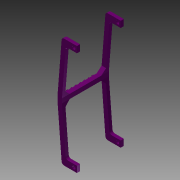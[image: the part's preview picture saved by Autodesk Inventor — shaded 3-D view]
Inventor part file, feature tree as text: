
AUTODESK INVENTOR PART (.ipt)
format: ipt  version: 2015 (Build 190159000, 159)  size: 382,464 bytes
history: native  units: mm
features: extrude x6, sketch x6, plane x2, mirror x2, fillet x1, projected_geometry x1
ambient origin geometry x8: Origin, YZ Plane, XZ Plane, XY Plane, X Axis, Y Axis, Z Axis, Center Point
bodies: Solid1 (feature_tree)
feature tree (18):
  extrude  "Extrusion1"  Depth=3.5mm
  extrude  "Extrusion2"  Depth=3.5mm
  fillet  "Fillet1"  Radius=3.5mm
  plane  "Work Plane2"
  extrude  "Extrusion3"  Depth=4.983674mm
  extrude  "Extrusion4"  Depth=2.5mm
  extrude  "Extrusion5"  Depth=2.5mm
  plane  "Work Plane3"
  mirror  "Mirror1"
  mirror  "Mirror2"
  extrude  "Extrusion6"  Depth=30.607599mm
  sketch  "Sketch3"  dims[d0=7.0mm d1=3.5mm]
  sketch  "Sketch4"  dims[d2=7.0mm d8=3.5mm d9=3.5mm]
  sketch  "Sketch6"  dims[d13=9.917653mm d14=4.983674mm]
  sketch  "Sketch7"  dims[d15=8.285585mm d17=2.5mm]
  sketch  "Sketch8"  dims[d18=90.0deg d19=2.5mm]
  sketch  "Sketch9"  dims[d21=5.0mm d22=30.607599mm d24=56.462921mm d25=49.462921mm d26=30.607599mm d27=16.516291mm d28=16.516291mm d29=2.8mm d30=2.8mm d31=5.0mm d32=3.5mm d33=0.0mm d34=5.0mm d35=5.0mm d36=22.75mm d37=0.0mm d38=0.25mm d40=-23.58913mm d41=5.0mm d42=0.0mm d43=45.0deg d44=7.0mm d45=0.0mm d46=7.0mm d47=0.0mm d48=7.0mm d49=0.0mm d50=0.0mm d51=52.5mm d52=1.823851mm d53=12.835531mm d54=1.5mm d55=0.0mm]
  projected_geometry  "Projected Loop2"
